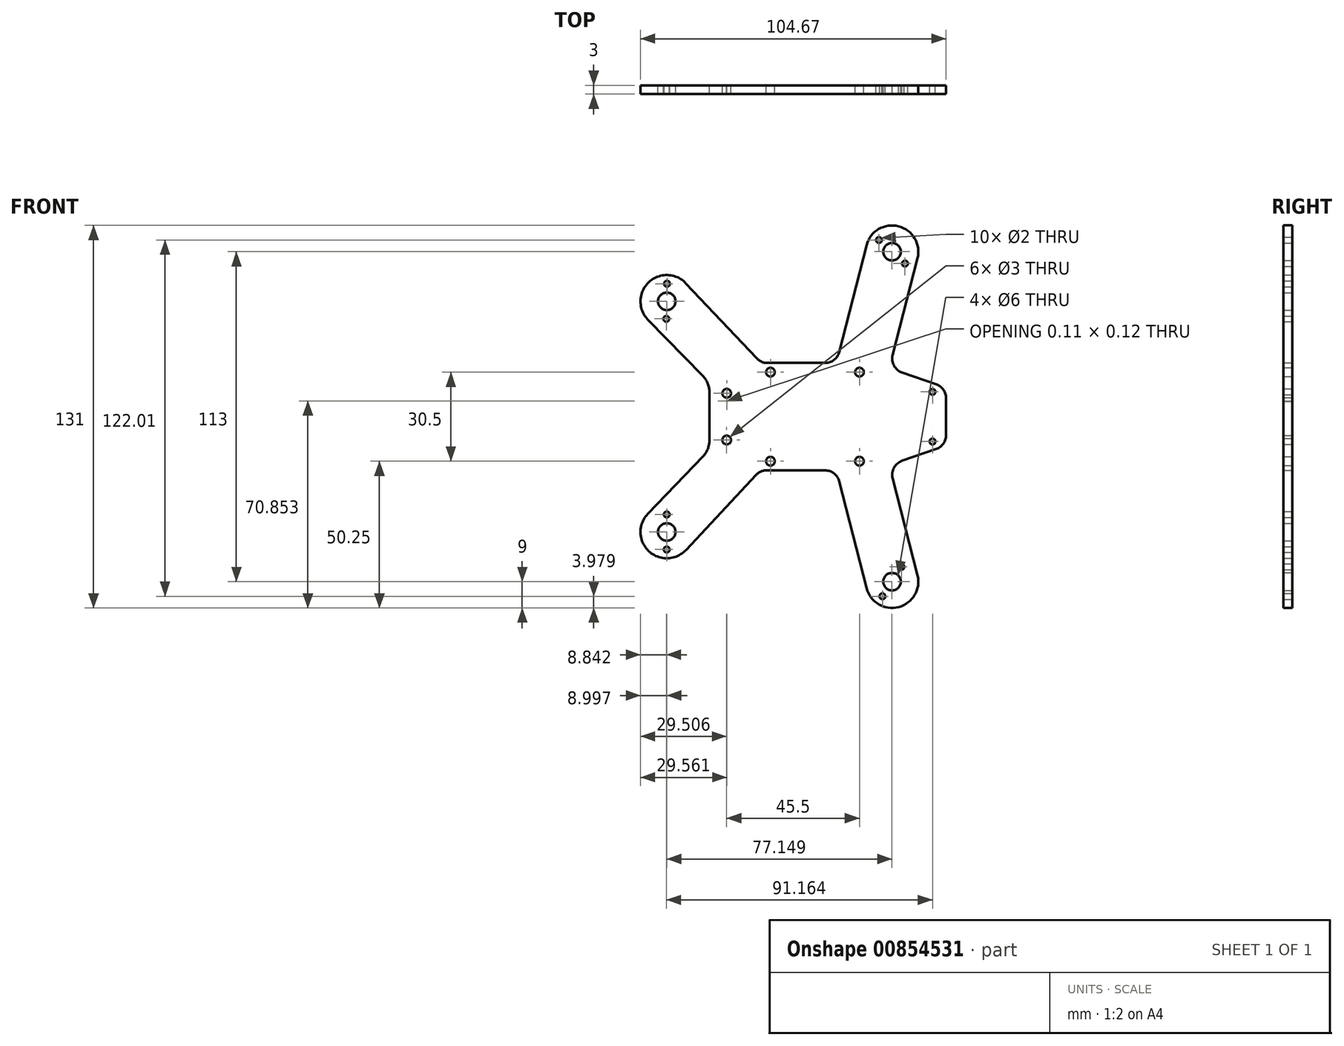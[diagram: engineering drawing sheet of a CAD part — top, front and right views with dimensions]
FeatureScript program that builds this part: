
annotation { "Feature Type Name" : "Feature", "Feature Type Description" : "" }
export const myFeature = defineFeature(function(context is Context, id is Id, definition is map)
    precondition{}
    {
        {
            var Q0;
            Q0=qCreatedBy(makeId("Front.planeOp"),FACE);
            var sketch = newSketch(context, id + "F0", { "sketchPlane" : qUnion([Q0])});
            skLineSegment(sketch, "E0.bottom", {"start": v(-3.88, -18.39) * mm, "end": v(-23.86, -18.39) * mm});
            skLineSegment(sketch, "E0.top", {"start": v(-3.88, 18.39) * mm, "end": v(-23.64, 18.39) * mm});
            skLineSegment(sketch, "E0.left", {"start": v(37.58, -6.33) * mm, "end": v(37.58, -5.89) * mm});
            skLineSegment(sketch, "E0.right", {"start": v(-37.58, -5.3) * mm, "end": v(-37.58, 5.3) * mm});
            skPoint(sketch, "E0.middle", {"position": v(0, 0) * mm});
            skPoint(sketch, "E1", {"position": v(-22.58, 15.25) * mm});
            skPoint(sketch, "E2", {"position": v(-22.58, -15.25) * mm});
            skPoint(sketch, "E3", {"position": v(7.92, 15.25) * mm});
            skPoint(sketch, "E4", {"position": v(7.92, -15.25) * mm});
            skPoint(sketch, "E5", {"position": v(32.92, 8.5) * mm});
            skPoint(sketch, "E6", {"position": v(32.92, -8.5) * mm});
            skCircle(sketch, "E7", {"center": v(-22.58, 15.25) * mm, "radius": 1.5 * mm});
            skCircle(sketch, "E8", {"center": v(-22.58, -15.25) * mm, "radius": 1.5 * mm});
            skCircle(sketch, "E9", {"center": v(7.92, 15.25) * mm, "radius": 1.5 * mm});
            skCircle(sketch, "E10", {"center": v(7.92, -15.25) * mm, "radius": 1.5 * mm});
            skCircle(sketch, "E11", {"center": v(32.92, 8.5) * mm, "radius": 1 * mm});
            skCircle(sketch, "E12", {"center": v(32.92, -8.5) * mm, "radius": 1 * mm});
            skArc(sketch, "E13", {"start": v(-37.47, 5.41) * mm, "mid": v(-37.53, 5.35) * mm, "end": v(-37.58, 5.3) * mm});
            skLineSegment(sketch, "E14", {"start": v(-37.47, 5.41) * mm, "end": v(-37.58, 5.3) * mm});
            skPoint(sketch, "E15.orphan", {"position": v(-37.58, 18.39) * mm});
            skPoint(sketch, "E16.orphan", {"position": v(-37.58, -18.39) * mm});
            skPoint(sketch, "E17", {"position": v(37.58, -9.89) * mm});
            skPoint(sketch, "E18", {"position": v(37.58, 9.89) * mm});
            skLineSegment(sketch, "E19", {"start": v(22.48, 15.14) * mm, "end": v(34.23, 11.05) * mm});
            skLineSegment(sketch, "E20", {"start": v(22.48, -15.14) * mm, "end": v(34.23, -11.05) * mm});
            skPoint(sketch, "E21.orphan", {"position": v(37.58, 18.39) * mm});
            skPoint(sketch, "E22.orphan", {"position": v(37.58, -18.39) * mm});
            skPoint(sketch, "E23", {"position": v(37.58, 5.89) * mm});
            skPoint(sketch, "E24", {"position": v(37.58, -5.89) * mm});
            skLineSegment(sketch, "E25.trimOffspring", {"start": v(37.58, 5.89) * mm, "end": v(37.58, 6.33) * mm});
            skPoint(sketch, "E26", {"position": v(-58.1, 39.5) * mm});
            skPoint(sketch, "E27", {"position": v(-58.1, -39.5) * mm});
            skPoint(sketch, "E28", {"position": v(19.06, -56.5) * mm});
            skPoint(sketch, "E29", {"position": v(19.06, 56.5) * mm});
            skPoint(sketch, "E30.center.orphan", {"position": v(-19.86, 0) * mm});
            skPoint(sketch, "E31.center.orphan", {"position": v(23.9, 0) * mm});
            skLineSegment(sketch, "E32", {"start": v(37.58, 5.89) * mm, "end": v(37.58, -5.89) * mm});
            skCircle(sketch, "E33", {"center": v(-58.1, -39.5) * mm, "radius": 3 * mm});
            skCircle(sketch, "E34", {"center": v(-58.1, 39.5) * mm, "radius": 3 * mm});
            skCircle(sketch, "E35", {"center": v(19.06, 56.5) * mm, "radius": 3 * mm});
            skCircle(sketch, "E36", {"center": v(19.06, -56.5) * mm, "radius": 3 * mm});
            skArc(sketch, "E37", {"start": v(-64.59, -33.27) * mm, "mid": v(-64.28, -46.03) * mm, "end": v(-51.52, -45.65) * mm});
            skArc(sketch, "E38", {"start": v(10.34, -58.73) * mm, "mid": v(21.29, -65.22) * mm, "end": v(27.77, -54.27) * mm});
            skArc(sketch, "E39", {"start": v(-51.55, 45.68) * mm, "mid": v(-64.33, 46) * mm, "end": v(-64.53, 33.21) * mm});
            skArc(sketch, "E40", {"start": v(27.77, 54.27) * mm, "mid": v(21.29, 65.22) * mm, "end": v(10.34, 58.73) * mm});
            skLineSegment(sketch, "E41", {"start": v(-45.75, 13.98) * mm, "end": v(-64.53, 33.21) * mm});
            skLineSegment(sketch, "E42", {"start": v(-27.27, 19.96) * mm, "end": v(-51.55, 45.68) * mm});
            skLineSegment(sketch, "E43", {"start": v(-27.52, -19.97) * mm, "end": v(-51.52, -45.65) * mm});
            skLineSegment(sketch, "E44", {"start": v(-45.7, -13.58) * mm, "end": v(-64.59, -33.27) * mm});
            skLineSegment(sketch, "E45", {"start": v(27.77, 54.27) * mm, "end": v(19.28, 21.1) * mm});
            skLineSegment(sketch, "E46", {"start": v(19.28, -21.1) * mm, "end": v(27.77, -54.27) * mm});
            skLineSegment(sketch, "E47", {"start": v(0.96, -22.15) * mm, "end": v(10.34, -58.73) * mm});
            skLineSegment(sketch, "E48", {"start": v(0.96, 22.15) * mm, "end": v(10.34, 58.73) * mm});
            skLineSegment(sketch, "E49", {"start": v(-43.47, 8.4) * mm, "end": v(-43.47, -8.04) * mm});
            skPoint(sketch, "E50.newPointA", {"position": v(13.14, -18.39) * mm});
            skPoint(sketch, "E50.newPointB", {"position": v(0, -18.39) * mm});
            skArc(sketch, "E50.filletArc", {"start": v(0.96, -22.15) * mm, "mid": v(-0.81, -19.44) * mm, "end": v(-3.88, -18.39) * mm});
            skPoint(sketch, "E51.newPointA", {"position": v(0, 18.39) * mm});
            skPoint(sketch, "E51.newPointB", {"position": v(13.14, 18.39) * mm});
            skArc(sketch, "E51.filletArc", {"start": v(-3.88, 18.39) * mm, "mid": v(-0.81, 19.44) * mm, "end": v(0.96, 22.15) * mm});
            skPoint(sketch, "E52.visualSharp", {"position": v(-25.8, 18.39) * mm});
            skArc(sketch, "E52.filletArc", {"start": v(-27.27, 19.96) * mm, "mid": v(-25.62, 18.8) * mm, "end": v(-23.64, 18.39) * mm});
            skPoint(sketch, "E53.visualSharp", {"position": v(-26.03, -18.39) * mm});
            skArc(sketch, "E53.filletArc", {"start": v(-23.86, -18.39) * mm, "mid": v(-25.85, -18.8) * mm, "end": v(-27.52, -19.97) * mm});
            skArc(sketch, "E54.filletArc", {"start": v(-45.7, -13.58) * mm, "mid": v(-44.05, -11.02) * mm, "end": v(-43.47, -8.04) * mm});
            skArc(sketch, "E55.filletArc", {"start": v(-43.47, 8.4) * mm, "mid": v(-44.06, 11.41) * mm, "end": v(-45.75, 13.98) * mm});
            skPoint(sketch, "E56.newPointA", {"position": v(18.14, 16.65) * mm});
            skArc(sketch, "E56.filletArc", {"start": v(19.28, 21.1) * mm, "mid": v(19.72, 17.5) * mm, "end": v(22.48, 15.14) * mm});
            skPoint(sketch, "E57.newPointB", {"position": v(18.14, -16.65) * mm});
            skArc(sketch, "E57.filletArc", {"start": v(22.48, -15.14) * mm, "mid": v(19.72, -17.5) * mm, "end": v(19.28, -21.1) * mm});
            skArc(sketch, "E58.filletArc", {"start": v(34.23, -11.05) * mm, "mid": v(36.66, -9.23) * mm, "end": v(37.58, -6.33) * mm});
            skArc(sketch, "E59.filletArc", {"start": v(37.58, 6.33) * mm, "mid": v(36.66, 9.23) * mm, "end": v(34.23, 11.05) * mm});
            skLineSegment(sketch, "E60", {"start": v(-37.56, 8) * mm, "end": v(-37.56, 0) * mm});
            skLineSegment(sketch, "E61", {"start": v(-37.56, 0) * mm, "end": v(-37.58, -8) * mm});
            skCircle(sketch, "E62", {"center": v(-37.56, 8) * mm, "radius": 1.5 * mm});
            skCircle(sketch, "E63", {"center": v(-37.58, -8) * mm, "radius": 1.5 * mm});
            skCircle(sketch, "E64", {"center": v(-58.02, 45.5) * mm, "radius": 1 * mm});
            skCircle(sketch, "E65", {"center": v(-58.25, 33.5) * mm, "radius": 1 * mm});
            skCircle(sketch, "E66", {"center": v(-58.1, -33.5) * mm, "radius": 1 * mm});
            skCircle(sketch, "E67", {"center": v(-58.1, -45.5) * mm, "radius": 1 * mm});
            skCircle(sketch, "E68", {"center": v(14.57, 60.49) * mm, "radius": 1 * mm});
            skCircle(sketch, "E69", {"center": v(23.49, 52.46) * mm, "radius": 1 * mm});
            skCircle(sketch, "E70", {"center": v(15.77, -61.52) * mm, "radius": 1 * mm});
            skCircle(sketch, "E71", {"center": v(22.24, -51.42) * mm, "radius": 1 * mm});
            skSolve(sketch);
        }
        {
            var Q0;
            Q0=makeQuery(id+"F0.imprint","IMPRINT",FACE,{"disambiguationData":[TD([[makeQuery(id+"F0.imprint","IMPRINT",EDGE,{"derivedFrom":sQuery(id+"F0.wireOp",EDGE,"E0.bottom")}),-1.0]])]});
            extrude(context, id + "F1", {"entities" : qUnion([Q0]), "depth" : 3 * mm, "offsetDistance" : 25 * mm});
        }
    });
